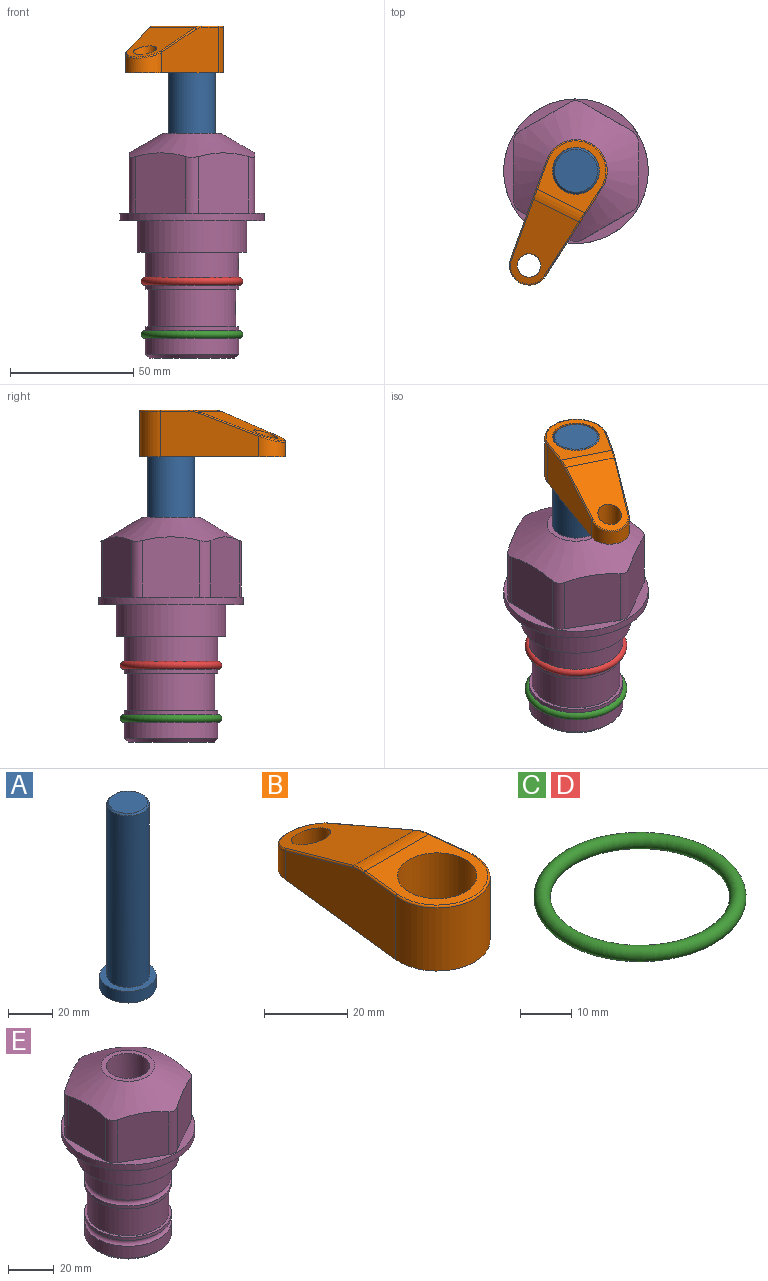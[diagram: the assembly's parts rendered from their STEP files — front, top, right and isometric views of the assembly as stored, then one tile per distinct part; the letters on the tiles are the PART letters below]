
ASSEMBLY  parts=5 mates=3
PART A: 6 faces, bbox 25.4x25.4x101.6 mm
  f0: plane 17.46x17.46mm, normal (0,0,1), area 239.5mm2, adj f5
  f1: plane 25.4x25.4mm, normal (0,0,-1), area 506.7mm2, adj f2
  f2: cylinder r=12.7mm len=25.4mm, axis (0,0,1), area 506.7mm2, adj f1,f3
  f3: plane 25.4x25.4mm, normal (0,0,1), area 221.7mm2, adj f2,f4
  f4: cylinder r=9.53mm len=94.46mm, axis (0,0,1), area 5653mm2, adj f3,f5
  f5: cone r=8.73mm half-angle=45deg, axis (0,0,-1), area 64.4mm2, adj f0,f4
PART B: 44 faces, bbox 27.5x64.5x19.1 mm
  f0: plane 2.3x0.95mm, normal (0,0,-1), area 1mm2, adj f25,f30,f34
  f1: plane 63.5x25.4mm, normal (0,0,-1), area 561.7mm2, adj f2,f3,f4,f5,f6,f7,f19,f20
  f2: cylinder r=12.7mm len=25.4mm, axis (0,0,-1), area 792.2mm2, adj f1,f3,f5,f13
  f3: plane 42.33x18.54mm, normal (0.99,0.11,0), area 647mm2, adj f1,f2,f4,f11,f12,f14
  f4: cylinder r=7.94mm len=15.78mm, axis (0,0,-1), area 158.6mm2, adj f1,f3,f5,f16
  f5: plane 42.33x18.54mm, normal (-0.99,0.11,0), area 647mm2, adj f1,f2,f4,f15,f17,f18
  f6: cylinder r=9.53mm len=19.05mm, axis (0,0,-1), area 1140.1mm2, adj f1,f8
  f7: cylinder r=4.76mm len=10.98mm, axis (0,0,-1), area 276.1mm2, adj f1,f9
  f8: plane 25.83x24.38mm, normal (0,0,1), area 262.2mm2, adj f6,f10,f11,f13,f15
  f9: plane 32.49x20.55mm, normal (0,0.34,0.94), area 489.9mm2, adj f7,f10,f14,f16,f18
  f10: cylinder r=12.7mm len=21.49mm, axis (-1,0,0), area 93.2mm2, adj f8,f9,f12,f17
  f11: cylinder r=0.51mm len=12.34mm, axis (0.11,-0.99,0), area 9.9mm2, adj f3,f8,f12,f13
  f12: bspline ~7.62x1.64mm, area 3.5mm2, adj f3,f10,f11,f14
  f13: torus R=12.19mm, axis (0,0,1), area 33.6mm2, adj f2,f8,f11,f15
  f14: cylinder r=0.51mm len=26.01mm, axis (0.1,-0.93,0.34), area 21.6mm2, adj f3,f9,f12,f16
  f15: cylinder r=0.51mm len=12.34mm, axis (0.11,0.99,0), area 9.9mm2, adj f5,f8,f13,f17
  f16: bspline ~15.78x7.05mm, area 15.7mm2, adj f4,f9,f14,f18
  f17: bspline ~7.62x1.64mm, area 3.5mm2, adj f5,f10,f15,f18
  f18: cylinder r=0.51mm len=26.01mm, axis (0.1,0.93,-0.34), area 21.6mm2, adj f5,f9,f16,f17
  f19: plane 21.6x14.29mm, normal (-0.99,-0.11,0), area 242.6mm2, adj f1,f26,f28,f34,f36,f38
  f20: plane 21.6x14.29mm, normal (0.99,-0.11,0), area 242.6mm2, adj f1,f27,f29,f37,f39,f41
  f21: cylinder r=12.7mm len=14.29mm, axis (0,0,-1), area 173.2mm2, adj f1,f26,f27,f30,f31,f33
  f22: cylinder r=7.94mm len=7.63mm, axis (0,0,-1), area 53.8mm2, adj f1,f28,f29,f42
  f23: plane 2.3x0.95mm, normal (0,0,-1), area 1mm2, adj f25,f33,f37
  f24: plane 17.94x12.32mm, normal (0,-0.34,-0.94), area 191.2mm2, adj f25,f38,f41,f42
  f25: cylinder r=9.53mm len=12.93mm, axis (-1,0,0), area 37.5mm2, adj f0,f23,f24,f31,f36,f39
  f26: cylinder r=1.59mm len=14.29mm, axis (0,0,-1), area 49mm2, adj f1,f19,f21,f32
  f27: cylinder r=1.59mm len=14.29mm, axis (0,0,-1), area 49mm2, adj f1,f20,f21,f35
  f28: cylinder r=1.59mm len=7.28mm, axis (0,0,-1), area 22.1mm2, adj f1,f19,f22,f40
  f29: cylinder r=1.59mm len=7.28mm, axis (0,0,-1), area 22.1mm2, adj f1,f20,f22,f43
  f30: torus R=14.29mm, axis (0,0,1), area 5.8mm2, adj f0,f21,f31,f32
  f31: bspline ~11.06x2.73mm, area 20.8mm2, adj f21,f25,f30,f33
  f32: sphere r=1.59mm, area 5.4mm2, adj f26,f30,f34
  f33: torus R=14.29mm, axis (0,0,1), area 5.8mm2, adj f21,f23,f31,f35
  f34: cylinder r=1.59mm len=1.68mm, axis (-0.11,0.99,0), area 2.4mm2, adj f0,f19,f32,f36
  f35: sphere r=1.59mm, area 5.4mm2, adj f27,f33,f37
  f36: bspline ~5.82x2.33mm, area 7.7mm2, adj f19,f25,f34,f38
  f37: cylinder r=1.59mm len=1.68mm, axis (0.11,0.99,0), area 2.4mm2, adj f20,f23,f35,f39
  f38: cylinder r=1.59mm len=18.33mm, axis (0.1,-0.93,0.34), area 46.7mm2, adj f19,f24,f36,f40
  f39: bspline ~5.82x2.33mm, area 7.7mm2, adj f20,f25,f37,f41
  f40: sphere r=1.59mm, area 3.6mm2, adj f28,f38,f42
  f41: cylinder r=1.59mm len=18.33mm, axis (0.1,0.93,-0.34), area 46.7mm2, adj f20,f24,f39,f43
  f42: bspline ~8.31x1.84mm, area 15.3mm2, adj f22,f24,f40,f43
  f43: sphere r=1.59mm, area 3.6mm2, adj f29,f41,f42
PART C: 1 faces, bbox 44.7x44.7x3.2 mm
  f0: torus R=19.05mm, axis (0,0,1), area 1193.9mm2
PART D: same geometry as C
PART E: 36 faces, bbox 58.7x58.7x91.2 mm
  f0: cylinder r=17.78mm len=35.56mm, axis (0,0,1), area 1670.8mm2, adj f23,f24,f31
  f1: cylinder r=19.05mm len=38.1mm, axis (0,0,1), area 1191.9mm2, adj f26,f27,f30
  f2: plane 58.66x58.66mm, normal (0,0,-1), area 1150.6mm2, adj f3,f28
  f3: cylinder r=29.33mm len=58.66mm, axis (0,0,-1), area 585.1mm2, adj f2,f4
  f4: plane 58.66x58.66mm, normal (0,0,1), area 475.9mm2, adj f3,f5,f6,f7,f8,f9,f10,f11
  f5: plane 24.5x20.32mm, normal (-0.5,0.87,0), area 562.8mm2, adj f4,f15,f16,f17
  f6: plane 24.5x20.32mm, normal (0.5,0.87,0), area 562.8mm2, adj f4,f14,f15,f17
  f7: plane 24.5x23.48mm, normal (1,0,0), area 562.8mm2, adj f4,f13,f14,f17
  f8: plane 24.5x20.32mm, normal (0.5,-0.87,0), area 562.8mm2, adj f4,f12,f13,f17
  f9: plane 24.5x20.32mm, normal (-0.5,-0.87,0), area 562.8mm2, adj f4,f11,f12,f17
  f10: plane 24.5x23.48mm, normal (-1,0,0), area 562.8mm2, adj f4,f11,f16,f17
  f11: cylinder r=5.08mm len=23.01mm, axis (0,0,-1), area 121.2mm2, adj f4,f9,f10,f17
  f12: cylinder r=5.08mm len=23.01mm, axis (0,0,-1), area 121.2mm2, adj f4,f8,f9,f17
  f13: cylinder r=5.08mm len=23.01mm, axis (0,0,-1), area 121.2mm2, adj f4,f7,f8,f17
  f14: cylinder r=5.08mm len=23.01mm, axis (0,0,-1), area 121.2mm2, adj f4,f6,f7,f17
  f15: cylinder r=5.08mm len=23.01mm, axis (0,0,-1), area 121.2mm2, adj f4,f5,f6,f17
  f16: cylinder r=5.08mm len=23.01mm, axis (0,0,-1), area 121.2mm2, adj f4,f5,f10,f17
  f17: cone r=11.73mm half-angle=60deg, axis (0,0,-1), area 2071.8mm2, adj f5,f6,f7,f8,f9,f10,f11,f12
  f18: plane 23.46x23.46mm, normal (0,0,1), area 147.4mm2, adj f17,f35
  f19: plane 34.93x34.93mm, normal (0,0,-1), area 958mm2, adj f29
  f20: cylinder r=19.05mm len=38.1mm, axis (0,0,1), area 760.1mm2, adj f21,f29
  f21: torus R=19.05mm, axis (0,0,1), area 565.3mm2, adj f20,f22
  f22: cylinder r=19.05mm len=38.1mm, axis (0,0,1), area 190mm2, adj f21,f23
  f23: plane 38.1x38.1mm, normal (0,0,1), area 146.9mm2, adj f0,f22
  f24: plane 38.1x38.1mm, normal (0,0,-1), area 146.9mm2, adj f0,f25
  f25: cylinder r=19.05mm len=38.1mm, axis (0,0,1), area 190mm2, adj f24,f26
  f26: torus R=19.05mm, axis (0,0,1), area 565.3mm2, adj f1,f25
  f27: plane 44.45x44.45mm, normal (0,0,-1), area 411.7mm2, adj f1,f28
  f28: cylinder r=22.23mm len=44.45mm, axis (0,0,1), area 1773.5mm2, adj f2,f27
  f29: cone r=19.05mm half-angle=45deg, axis (0,0,1), area 257.5mm2, adj f19,f20
  f30: cylinder r=3.17mm len=6.75mm, axis (-1,0,0), area 128mm2, adj f1,f33
  f31: cylinder r=3.17mm len=6.35mm, axis (-1,0,0), area 102.5mm2, adj f0,f33
  f32: plane 25.4x25.4mm, normal (0,0,1), area 506.7mm2, adj f33
  f33: cylinder r=12.7mm len=66.42mm, axis (0,0,-1), area 5236.2mm2, adj f30,f31,f32,f34
  f34: cone r=9.53mm half-angle=30deg, axis (0,0,-1), area 443.4mm2, adj f33,f35
  f35: cylinder r=9.53mm len=19.05mm, axis (0,0,-1), area 849mm2, adj f18,f34
PLACE A rot(axis=(0,0,-1),116.4deg) t=(0,0,5.49)mm
PLACE B rot(axis=(0,0,1),153.6deg) t=(0,0,60.1)mm
PLACE C t=(0,0,-21.59)mm
PLACE D at identity
PLACE E at identity fixed
MATE fastened C.f0 <-> E.f0  axis (0,0,1) through (0,0,-46.1)mm
MATE cylindrical A.f2 <-> E.f0  axis (0,0,1) through (0,0,31.13)mm
MATE fastened B.f2 <-> A.f2  axis (0,0,1) through (0,0,79.15)mm
